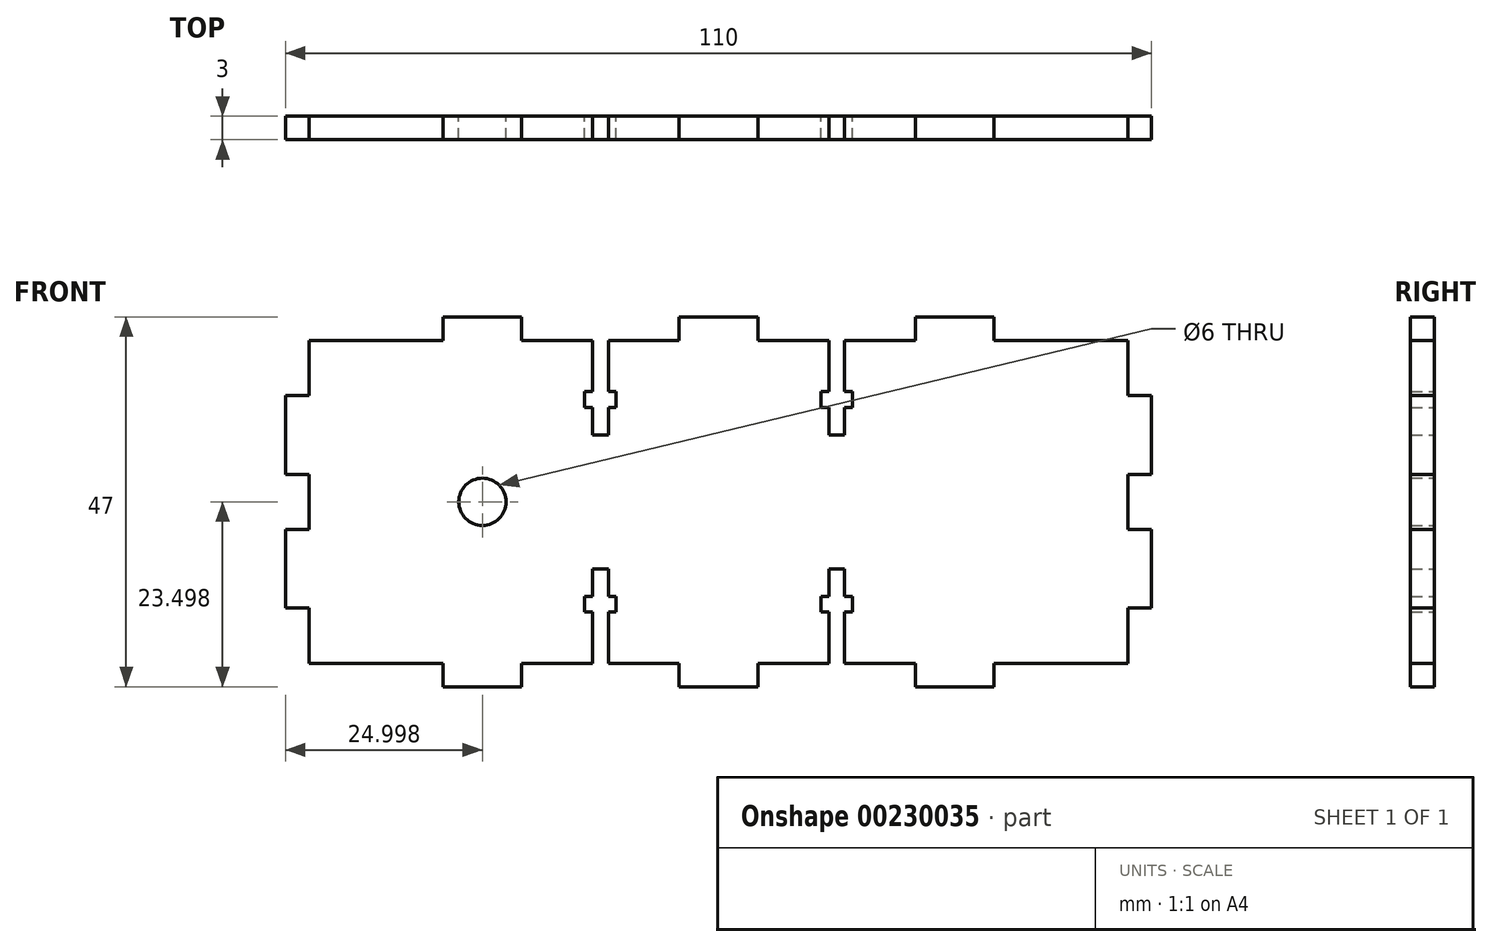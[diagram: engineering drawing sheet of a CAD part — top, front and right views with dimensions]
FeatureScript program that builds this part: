
annotation { "Feature Type Name" : "Feature", "Feature Type Description" : "" }
export const myFeature = defineFeature(function(context is Context, id is Id, definition is map)
    precondition{}
    {
        {
            var Q0;
            Q0=qCreatedBy(makeId("Front.planeOp"),FACE);
            var sketch = newSketch(context, id + "F0", { "sketchPlane" : qUnion([Q0])});
            skLineSegment(sketch, "E0", {"start": v(-56.01, 8.9) * mm, "end": v(-47.01, 8.9) * mm});
            skLineSegment(sketch, "E1", {"start": v(-47.01, 8.9) * mm, "end": v(-47.01, 2.4) * mm});
            skLineSegment(sketch, "E2", {"start": v(-47.01, 2.4) * mm, "end": v(-48.01, 2.4) * mm});
            skLineSegment(sketch, "E3", {"start": v(-48.01, 2.4) * mm, "end": v(-48.01, 0.4) * mm});
            skLineSegment(sketch, "E4", {"start": v(-48.01, 0.4) * mm, "end": v(-47.01, 0.4) * mm});
            skLineSegment(sketch, "E5", {"start": v(-47.01, 0.4) * mm, "end": v(-47.01, -3.1) * mm});
            skLineSegment(sketch, "E6", {"start": v(-47.01, -3.1) * mm, "end": v(-45.01, -3.1) * mm});
            skLineSegment(sketch, "E7", {"start": v(-45.01, -3.1) * mm, "end": v(-45.01, 0.4) * mm});
            skLineSegment(sketch, "E8", {"start": v(-45.01, 0.4) * mm, "end": v(-44.01, 0.4) * mm});
            skLineSegment(sketch, "E9", {"start": v(-44.01, 0.4) * mm, "end": v(-44.01, 2.4) * mm});
            skLineSegment(sketch, "E10", {"start": v(-44.01, 2.4) * mm, "end": v(-45.01, 2.4) * mm});
            skLineSegment(sketch, "E11", {"start": v(-45.01, 2.4) * mm, "end": v(-45.01, 8.9) * mm});
            skLineSegment(sketch, "E12", {"start": v(-45.01, 8.9) * mm, "end": v(-36.01, 8.9) * mm});
            skLineSegment(sketch, "E13", {"start": v(-36.01, 11.9) * mm, "end": v(-36.01, 8.9) * mm});
            skLineSegment(sketch, "E14", {"start": v(-36.01, 11.9) * mm, "end": v(-31.01, 11.9) * mm});
            skLineSegment(sketch, "E15", {"start": v(-56.01, 8.9) * mm, "end": v(-56.01, 11.9) * mm});
            skLineSegment(sketch, "E16", {"start": v(-56.01, 11.9) * mm, "end": v(-66.01, 11.9) * mm});
            skLineSegment(sketch, "E17", {"start": v(-66.01, 11.9) * mm, "end": v(-66.01, 8.9) * mm});
            skLineSegment(sketch, "E18", {"start": v(-66.01, 8.9) * mm, "end": v(-83.01, 8.9) * mm});
            skLineSegment(sketch, "E19", {"start": v(-83.01, 8.9) * mm, "end": v(-83.01, 1.9) * mm});
            skLineSegment(sketch, "E20", {"start": v(-83.01, 1.9) * mm, "end": v(-86.01, 1.9) * mm});
            skLineSegment(sketch, "E21", {"start": v(-86.01, 1.9) * mm, "end": v(-86.01, -8.1) * mm});
            skLineSegment(sketch, "E22", {"start": v(-86.01, -8.1) * mm, "end": v(-83.01, -8.1) * mm});
            skLineSegment(sketch, "E23", {"start": v(-83.01, -8.1) * mm, "end": v(-83.01, -11.6) * mm});
            skLineSegment(sketch, "E24", {"start": v(-83.01, -11.6) * mm, "end": v(-31.01, -11.6) * mm, "construction": true});
            skLineSegment(sketch, "E25.MirrorCS", {"start": v(-45.01, -23.6) * mm, "end": v(-44.01, -23.6) * mm});
            skLineSegment(sketch, "E26.MirrorCS", {"start": v(-44.01, -23.6) * mm, "end": v(-44.01, -25.6) * mm});
            skLineSegment(sketch, "E27.MirrorCS", {"start": v(-44.01, -25.6) * mm, "end": v(-45.01, -25.6) * mm});
            skLineSegment(sketch, "E28.MirrorCS", {"start": v(-47.01, -20.1) * mm, "end": v(-45.01, -20.1) * mm});
            skLineSegment(sketch, "E29.MirrorCS", {"start": v(-48.01, -23.6) * mm, "end": v(-47.01, -23.6) * mm});
            skLineSegment(sketch, "E30.MirrorCS", {"start": v(-47.01, -25.6) * mm, "end": v(-48.01, -25.6) * mm});
            skLineSegment(sketch, "E31.MirrorCS", {"start": v(-48.01, -25.6) * mm, "end": v(-48.01, -23.6) * mm});
            skLineSegment(sketch, "E32.MirrorCS", {"start": v(-86.01, -15.1) * mm, "end": v(-83.01, -15.1) * mm});
            skLineSegment(sketch, "E33.MirrorCS", {"start": v(-83.01, -25.1) * mm, "end": v(-86.01, -25.1) * mm});
            skLineSegment(sketch, "E34.MirrorCS", {"start": v(-47.01, -23.6) * mm, "end": v(-47.01, -20.1) * mm});
            skLineSegment(sketch, "E35.MirrorCS", {"start": v(-45.01, -20.1) * mm, "end": v(-45.01, -23.6) * mm});
            skLineSegment(sketch, "E36.MirrorCS", {"start": v(-56.01, -35.1) * mm, "end": v(-66.01, -35.1) * mm});
            skLineSegment(sketch, "E37.MirrorCS", {"start": v(-66.01, -32.1) * mm, "end": v(-83.01, -32.1) * mm});
            skLineSegment(sketch, "E38.MirrorCS", {"start": v(-47.01, -32.1) * mm, "end": v(-47.01, -25.6) * mm});
            skLineSegment(sketch, "E39.MirrorCS", {"start": v(-56.01, -32.1) * mm, "end": v(-47.01, -32.1) * mm});
            skLineSegment(sketch, "E40.MirrorCS", {"start": v(-56.01, -32.1) * mm, "end": v(-56.01, -35.1) * mm});
            skLineSegment(sketch, "E41.MirrorCS", {"start": v(-36.01, -35.1) * mm, "end": v(-31.01, -35.1) * mm});
            skLineSegment(sketch, "E42.MirrorCS", {"start": v(-36.01, -35.1) * mm, "end": v(-36.01, -32.1) * mm});
            skLineSegment(sketch, "E43.MirrorCS", {"start": v(-66.01, -35.1) * mm, "end": v(-66.01, -32.1) * mm});
            skLineSegment(sketch, "E44.MirrorCS", {"start": v(-83.01, -32.1) * mm, "end": v(-83.01, -25.1) * mm});
            skLineSegment(sketch, "E45.MirrorCS", {"start": v(-83.01, -15.1) * mm, "end": v(-83.01, -11.6) * mm});
            skLineSegment(sketch, "E46.MirrorCS", {"start": v(-45.01, -32.1) * mm, "end": v(-36.01, -32.1) * mm});
            skLineSegment(sketch, "E47.MirrorCS", {"start": v(-45.01, -25.6) * mm, "end": v(-45.01, -32.1) * mm});
            skLineSegment(sketch, "E48.MirrorCS", {"start": v(-86.01, -25.1) * mm, "end": v(-86.01, -15.1) * mm});
            skLineSegment(sketch, "E49", {"start": v(-31.01, 11.9) * mm, "end": v(-31.01, -35.1) * mm, "construction": true});
            skLineSegment(sketch, "E50.MirrorCS", {"start": v(-15.01, 2.4) * mm, "end": v(-14.01, 2.4) * mm});
            skLineSegment(sketch, "E51.MirrorCS", {"start": v(-17.01, 0.4) * mm, "end": v(-18.01, 0.4) * mm});
            skLineSegment(sketch, "E52.MirrorCS", {"start": v(-18.01, -25.6) * mm, "end": v(-17.01, -25.6) * mm});
            skLineSegment(sketch, "E53.MirrorCS", {"start": v(-14.01, -23.6) * mm, "end": v(-15.01, -23.6) * mm});
            skLineSegment(sketch, "E54.MirrorCS", {"start": v(-18.01, -23.6) * mm, "end": v(-18.01, -25.6) * mm});
            skLineSegment(sketch, "E55.MirrorCS", {"start": v(-14.01, 2.4) * mm, "end": v(-14.01, 0.4) * mm});
            skLineSegment(sketch, "E56.MirrorCS", {"start": v(-14.01, 0.4) * mm, "end": v(-15.01, 0.4) * mm});
            skLineSegment(sketch, "E57.MirrorCS", {"start": v(-15.01, -3.1) * mm, "end": v(-17.01, -3.1) * mm});
            skLineSegment(sketch, "E58.MirrorCS", {"start": v(-18.01, 0.4) * mm, "end": v(-18.01, 2.4) * mm});
            skLineSegment(sketch, "E59.MirrorCS", {"start": v(-18.01, 2.4) * mm, "end": v(-17.01, 2.4) * mm});
            skLineSegment(sketch, "E60.MirrorCS", {"start": v(-15.01, -20.1) * mm, "end": v(-17.01, -20.1) * mm});
            skLineSegment(sketch, "E61.MirrorCS", {"start": v(-15.01, -25.6) * mm, "end": v(-14.01, -25.6) * mm});
            skLineSegment(sketch, "E62.MirrorCS", {"start": v(-14.01, -25.6) * mm, "end": v(-14.01, -23.6) * mm});
            skLineSegment(sketch, "E63.MirrorCS", {"start": v(-17.01, -23.6) * mm, "end": v(-18.01, -23.6) * mm});
            skLineSegment(sketch, "E64.MirrorCS", {"start": v(-15.01, 0.4) * mm, "end": v(-15.01, -3.1) * mm});
            skLineSegment(sketch, "E65.MirrorCS", {"start": v(-15.01, -23.6) * mm, "end": v(-15.01, -20.1) * mm});
            skLineSegment(sketch, "E66.MirrorCS", {"start": v(-26.01, -35.1) * mm, "end": v(-26.01, -32.1) * mm});
            skLineSegment(sketch, "E67.MirrorCS", {"start": v(20.99, 8.9) * mm, "end": v(20.99, 1.9) * mm});
            skLineSegment(sketch, "E68.MirrorCS", {"start": v(-17.01, -20.1) * mm, "end": v(-17.01, -23.6) * mm});
            skLineSegment(sketch, "E69.MirrorCS", {"start": v(-26.01, 11.9) * mm, "end": v(-26.01, 8.9) * mm});
            skLineSegment(sketch, "E70.MirrorCS", {"start": v(-26.01, 11.9) * mm, "end": v(-31.01, 11.9) * mm});
            skLineSegment(sketch, "E71.MirrorCS", {"start": v(-6.01, 8.9) * mm, "end": v(-6.01, 11.9) * mm});
            skLineSegment(sketch, "E72.MirrorCS", {"start": v(-6.01, 8.9) * mm, "end": v(-15.01, 8.9) * mm});
            skLineSegment(sketch, "E73.MirrorCS", {"start": v(-15.01, 8.9) * mm, "end": v(-15.01, 2.4) * mm});
            skLineSegment(sketch, "E74.MirrorCS", {"start": v(-17.01, -3.1) * mm, "end": v(-17.01, 0.4) * mm});
            skLineSegment(sketch, "E75.MirrorCS", {"start": v(-17.01, 2.4) * mm, "end": v(-17.01, 8.9) * mm});
            skLineSegment(sketch, "E76.MirrorCS", {"start": v(3.99, -35.1) * mm, "end": v(3.99, -32.1) * mm});
            skLineSegment(sketch, "E77.MirrorCS", {"start": v(-17.01, 8.9) * mm, "end": v(-26.01, 8.9) * mm});
            skLineSegment(sketch, "E78.MirrorCS", {"start": v(-6.01, -32.1) * mm, "end": v(-15.01, -32.1) * mm});
            skLineSegment(sketch, "E79.MirrorCS", {"start": v(20.99, -8.1) * mm, "end": v(20.99, -11.6) * mm});
            skLineSegment(sketch, "E80.MirrorCS", {"start": v(20.99, 1.9) * mm, "end": v(23.99, 1.9) * mm});
            skLineSegment(sketch, "E81.MirrorCS", {"start": v(20.99, -15.1) * mm, "end": v(20.99, -11.6) * mm});
            skLineSegment(sketch, "E82.MirrorCS", {"start": v(20.99, -32.1) * mm, "end": v(20.99, -25.1) * mm});
            skLineSegment(sketch, "E83.MirrorCS", {"start": v(-6.01, -32.1) * mm, "end": v(-6.01, -35.1) * mm});
            skLineSegment(sketch, "E84.MirrorCS", {"start": v(20.99, -11.6) * mm, "end": v(-31.01, -11.6) * mm, "construction": true});
            skLineSegment(sketch, "E85.MirrorCS", {"start": v(23.99, 1.9) * mm, "end": v(23.99, -8.1) * mm});
            skLineSegment(sketch, "E86.MirrorCS", {"start": v(-17.01, -32.1) * mm, "end": v(-26.01, -32.1) * mm});
            skLineSegment(sketch, "E87.MirrorCS", {"start": v(20.99, -25.1) * mm, "end": v(23.99, -25.1) * mm});
            skLineSegment(sketch, "E88.MirrorCS", {"start": v(-15.01, -32.1) * mm, "end": v(-15.01, -25.6) * mm});
            skLineSegment(sketch, "E89.MirrorCS", {"start": v(-17.01, -25.6) * mm, "end": v(-17.01, -32.1) * mm});
            skLineSegment(sketch, "E90.MirrorCS", {"start": v(23.99, -8.1) * mm, "end": v(20.99, -8.1) * mm});
            skLineSegment(sketch, "E91.MirrorCS", {"start": v(-26.01, -35.1) * mm, "end": v(-31.01, -35.1) * mm});
            skLineSegment(sketch, "E92.MirrorCS", {"start": v(23.99, -15.1) * mm, "end": v(20.99, -15.1) * mm});
            skLineSegment(sketch, "E93.MirrorCS", {"start": v(23.99, -25.1) * mm, "end": v(23.99, -15.1) * mm});
            skLineSegment(sketch, "E94.MirrorCS", {"start": v(-6.01, -35.1) * mm, "end": v(3.99, -35.1) * mm});
            skLineSegment(sketch, "E95.MirrorCS", {"start": v(-6.01, 11.9) * mm, "end": v(3.99, 11.9) * mm});
            skLineSegment(sketch, "E96.MirrorCS", {"start": v(3.99, 8.9) * mm, "end": v(20.99, 8.9) * mm});
            skLineSegment(sketch, "E97.MirrorCS", {"start": v(3.99, 11.9) * mm, "end": v(3.99, 8.9) * mm});
            skLineSegment(sketch, "E98.MirrorCS", {"start": v(3.99, -32.1) * mm, "end": v(20.99, -32.1) * mm});
            skLineSegment(sketch, "E99", {"start": v(-61.01, 11.9) * mm, "end": v(-61.01, -35.1) * mm, "construction": true});
            skCircle(sketch, "E100", {"center": v(-61.01, -11.6) * mm, "radius": 3 * mm});
            skSolve(sketch);
        }
        {
            var Q0;
            Q0=makeQuery(id+"F0.imprint","IMPRINT",FACE,{"disambiguationData":[TD([[makeQuery(id+"F0.imprint","IMPRINT",EDGE,{"derivedFrom":sQuery(id+"F0.wireOp",EDGE,"E0")}),-1.0]])]});
            extrude(context, id + "F1", {"entities" : qUnion([Q0]), "depth" : 3 * mm});
        }
    });
